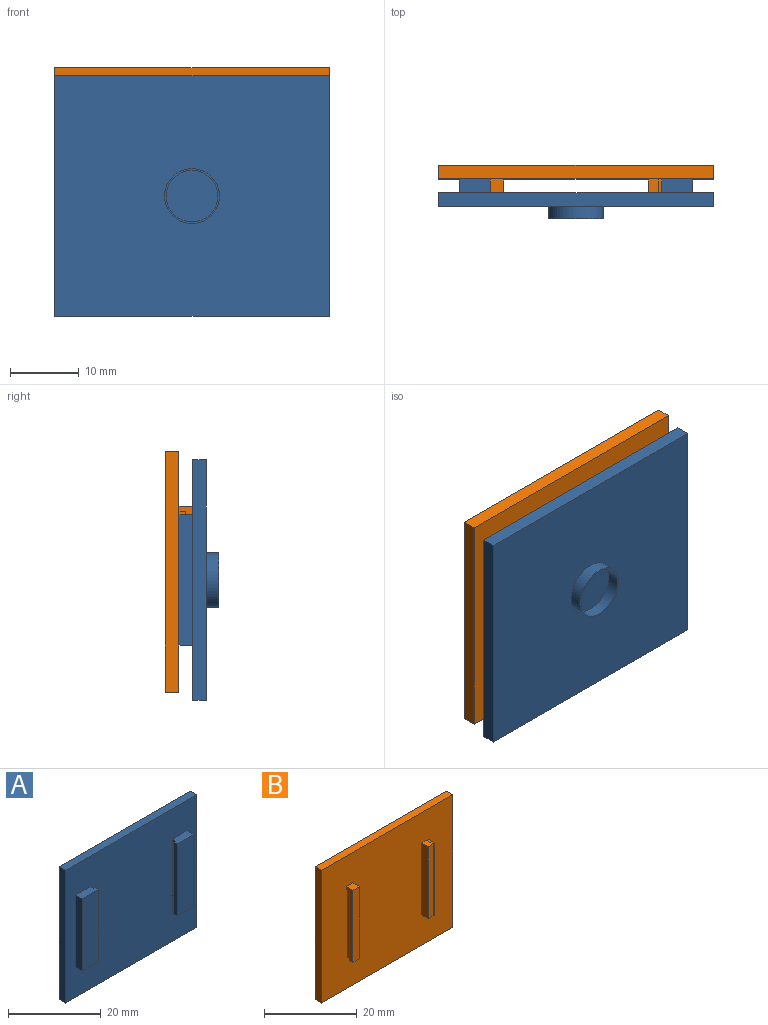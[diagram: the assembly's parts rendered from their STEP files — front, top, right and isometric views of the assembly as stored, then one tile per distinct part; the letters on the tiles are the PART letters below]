
ASSEMBLY  parts=2 mates=1
PART A: 24 faces, bbox 40x5.8x35 mm
  f0: plane 40x2mm, normal (0,0,-1), area 80mm2, adj f1,f3,f4,f5
  f1: plane 35x2mm, normal (1,0,0), area 70mm2, adj f0,f2,f4,f5
  f2: plane 40x2mm, normal (0,0,1), area 80mm2, adj f1,f3,f4,f5
  f3: plane 35x2mm, normal (-1,0,0), area 70mm2, adj f0,f2,f4,f5
  f4: plane 40x35mm, normal (0,1,0), area 1349.7mm2, adj f0,f1,f2,f3,f21
  f5: plane 40x35mm, normal (0,-1,0), area 1229mm2, adj f0,f1,f2,f3,f6,f7,f8,f10
  f6: plane 5x2mm, normal (0,0,1), area 9.5mm2, adj f5,f8,f9,f16,f17,f18
  f7: plane 5x2mm, normal (0,0,-1), area 9.5mm2, adj f5,f8,f9,f16,f17,f18
  f8: plane 19x2mm, normal (1,0,0), area 38mm2, adj f5,f6,f7,f9
  f9: plane 19x5mm, normal (0,-1,0), area 95mm2, adj f6,f7,f8,f17
  f10: plane 5x2mm, normal (0,0,1), area 9.5mm2, adj f5,f11,f13,f14,f15,f19
  f11: plane 19x2mm, normal (-1,0,0), area 38mm2, adj f5,f10,f12,f13
  f12: plane 5x2mm, normal (0,0,-1), area 9.5mm2, adj f5,f11,f13,f14,f15,f19
  f13: plane 19x5mm, normal (0,-1,0), area 95mm2, adj f10,f11,f12,f15
  f14: plane 19x0.5mm, normal (0,1,0), area 9.5mm2, adj f10,f12,f15,f19
  f15: plane 19x1mm, normal (1,0,0), area 19mm2, adj f10,f12,f13,f14
  f16: plane 19x0.5mm, normal (0,1,0), area 9.5mm2, adj f6,f7,f17,f18
  f17: plane 19x1mm, normal (-1,0,0), area 19mm2, adj f6,f7,f9,f16
  f18: plane 19x1mm, normal (-1,0,0), area 19mm2, adj f5,f6,f7,f16
  f19: plane 19x1mm, normal (1,0,0), area 19mm2, adj f5,f10,f12,f14
  f20: cylinder r=3.75mm len=7.5mm, axis (0,-1,0), area 42.4mm2, adj f22,f23
  f21: cylinder r=4mm len=8mm, axis (0,-1,0), area 45.2mm2, adj f4,f22
  f22: plane 8x8mm, normal (0,1,0), area 6.1mm2, adj f20,f21
  f23: plane 7.5x7.5mm, normal (0,1,0), area 44.2mm2, adj f20
PART B: 25 faces, bbox 40x4x35 mm
  f0: plane 40x35mm, normal (0,-1,0), area 1342mm2, adj f1,f2,f3,f4,f6,f7,f8,f9
  f1: plane 35x2mm, normal (-1,0,0), area 70mm2, adj f0,f2,f4,f5
  f2: plane 40x2mm, normal (0,0,-1), area 80mm2, adj f0,f1,f3,f5
  f3: plane 35x2mm, normal (1,0,0), area 70mm2, adj f0,f2,f4,f5
  f4: plane 40x2mm, normal (0,0,1), area 80mm2, adj f0,f1,f3,f5
  f5: plane 40x35mm, normal (0,1,0), area 1400mm2, adj f1,f2,f3,f4
  f6: plane 17.78x1mm, normal (1,0,0), area 17.8mm2, adj f0,f9,f17,f18
  f7: plane 2x1.5mm, normal (0,0,1), area 3mm2, adj f0,f8,f10,f19
  f8: plane 19x2mm, normal (-1,0,0), area 38mm2, adj f0,f7,f9,f10
  f9: plane 2x1.5mm, normal (0,0,-1), area 3mm2, adj f0,f6,f8,f10,f16
  f10: plane 19x1.5mm, normal (0,-1,0), area 28.5mm2, adj f7,f8,f9,f20
  f11: plane 18.29x1mm, normal (-1,0,0), area 18.3mm2, adj f0,f12,f22,f23
  f12: plane 2x2mm, normal (0,0,-1), area 3.5mm2, adj f0,f11,f13,f15,f23,f24
  f13: plane 19x2mm, normal (1,0,0), area 38mm2, adj f0,f12,f14,f15
  f14: plane 2x2mm, normal (0,0,1), area 4mm2, adj f0,f13,f15,f24
  f15: plane 19x2mm, normal (0,-1,0), area 38mm2, adj f12,f13,f14,f24
  f16: plane 1.05x0.5mm, normal (-0.05,0,-1), area 0.5mm2, adj f9,f17,f20,f21
  f17: plane 17.8x0.5mm, normal (-0.05,1,0), area 8.9mm2, adj f6,f16,f18,f21
  f18: plane 1x0.5mm, normal (-0.05,0,-1), area 0.5mm2, adj f0,f6,f17,f21
  f19: plane 2.03x0.5mm, normal (-0.05,0,1), area 1mm2, adj f0,f7,f20,f21
  f20: plane 19.05x0.5mm, normal (-0.05,-1,0), area 9.5mm2, adj f10,f16,f19,f21
  f21: plane 19.05x2.03mm, normal (1,0,0), area 21.3mm2, adj f0,f16,f17,f18,f19,f20
  f22: plane 1x0.5mm, normal (0,0,-1), area 0.5mm2, adj f0,f11,f23,f24
  f23: plane 18.29x0.5mm, normal (0,1,0), area 9.1mm2, adj f11,f12,f22,f24
  f24: plane 19x2mm, normal (-1,0,0), area 19.7mm2, adj f0,f12,f14,f15,f22,f23
PLACE A rot(axis=(0,0,1),180deg) t=(-6.06,-3.11,-0.23)mm
PLACE B t=(-6.06,-1.11,0.97)mm fixed
MATE slider A.f12 <-> B.f9  axis (0,0,-1) through (5.94,-1.61,-9.73)mm
